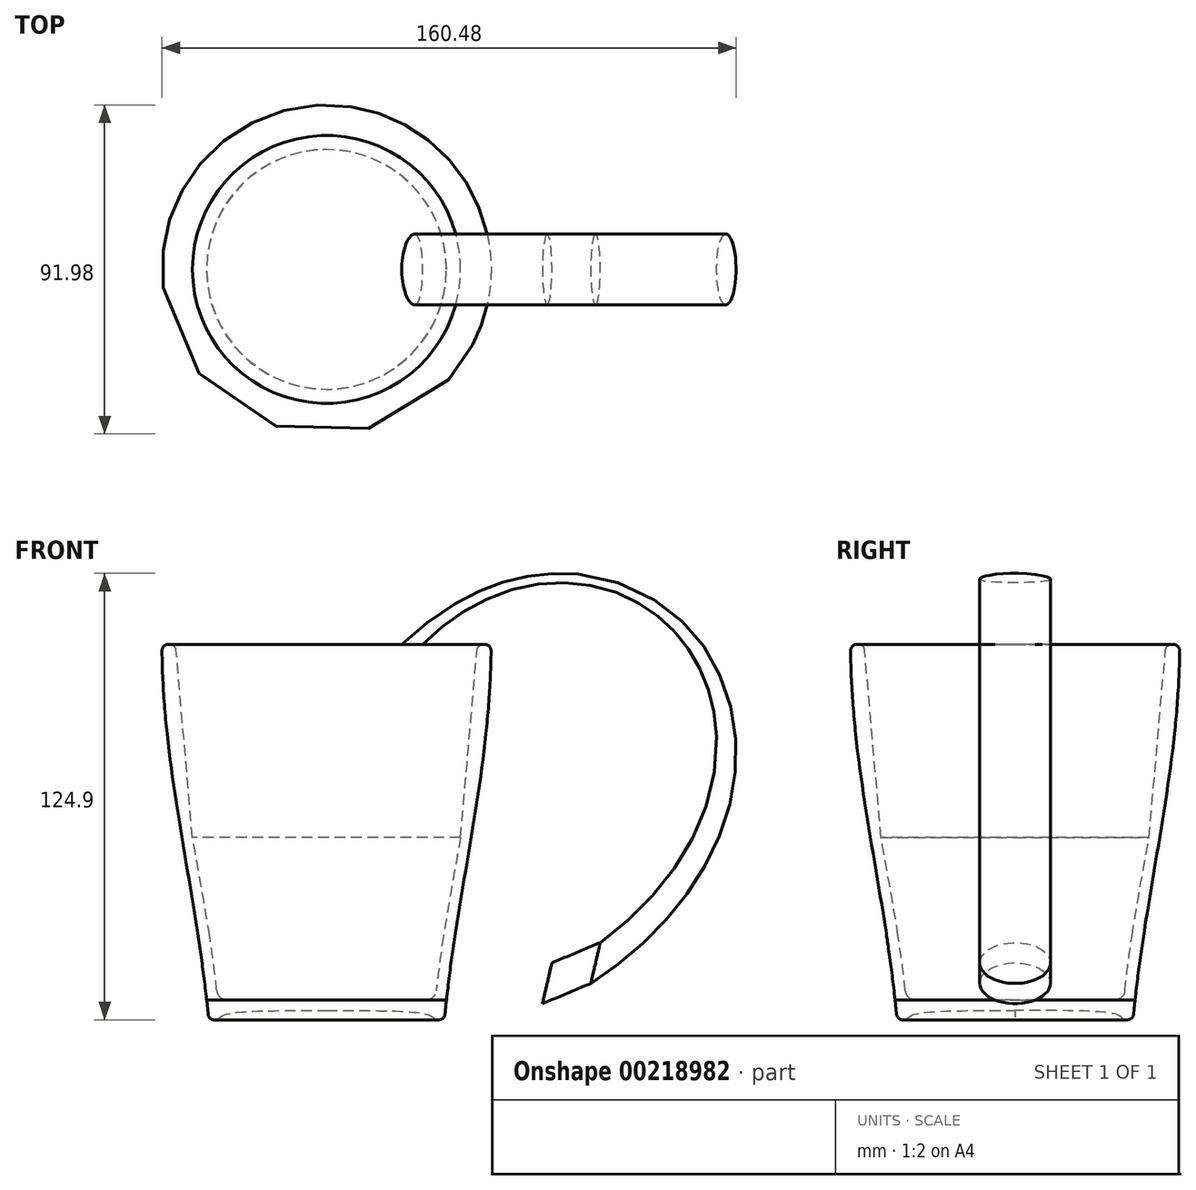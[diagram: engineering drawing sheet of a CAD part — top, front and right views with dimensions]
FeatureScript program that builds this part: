
annotation { "Feature Type Name" : "Feature", "Feature Type Description" : "" }
export const myFeature = defineFeature(function(context is Context, id is Id, definition is map)
    precondition{}
    {
        {
            assignVariable(context, id + "F0", {"name" : "handletop_r", "anyValue" : 4.46});
        }
        {
            var Q0;
            Q0=qCreatedBy(makeId("Front.planeOp"),FACE);
            var sketch = newSketch(context, id + "F1", { "sketchPlane" : qUnion([Q0])});
            skLineSegment(sketch, "E0.bottom", {"start": v(46, 52.5) * mm, "end": v(-46, 52.5) * mm});
            skLineSegment(sketch, "E0.top", {"start": v(46, -52.5) * mm, "end": v(-46, -52.5) * mm});
            skLineSegment(sketch, "E0.left", {"start": v(46, 52.5) * mm, "end": v(46, -52.5) * mm});
            skLineSegment(sketch, "E0.right", {"start": v(-46, 52.5) * mm, "end": v(-46, -52.5) * mm});
            skPoint(sketch, "E0.middle", {"position": v(0, 0) * mm});
            skLineSegment(sketch, "E1", {"start": v(33, -52.5) * mm, "end": v(46, 96.1) * mm});
            skFitSpline(sketch, "E2", {"points": [v(46, 52.5) * mm, v(33, -52.5) * mm], "startDerivative": vector(0, -106.58) * mm, "endDerivative": vector(-9.22, -105.38) * mm});
            skLineSegment(sketch, "E3.0", {"start": v(46, -49.9) * mm, "end": v(-46, -49.9) * mm});
            skLineSegment(sketch, "E4", {"start": v(0, 52.5) * mm, "end": v(0, -52.5) * mm});
            skLineSegment(sketch, "E5", {"start": v(30, -52.5) * mm, "end": v(30, -49.9) * mm});
            skFitSpline(sketch, "E6", {"points": [v(0, -49.9) * mm, v(30, -52.5) * mm], "startDerivative": vector(61.82, 0) * mm, "endDerivative": vector(0, -7.8) * mm});
            skFitSpline(sketch, "E7.0", {"points": [v(43, 52.5) * mm, v(43, 43.76) * mm, v(41.78, 26.36) * mm, v(37.8, 0.35) * mm, v(33.2, -25.76) * mm, v(30.79, -43.36) * mm, v(30.01, -52.24) * mm]});
            skLineSegment(sketch, "E8.0", {"start": v(46, -46.9) * mm, "end": v(-46, -46.9) * mm});
            skFitSpline(sketch, "E9", {"points": [v(44.56, 27.5) * mm, v(36.14, -27.5) * mm], "startDerivative": vector(116.8, 84.4) * mm, "endDerivative": vector(-197.13, -82.5) * mm});
            skLineSegment(sketch, "E10", {"start": v(44.56, 27.5) * mm, "end": v(30.84, 17.59) * mm});
            skLineSegment(sketch, "E11", {"start": v(36.14, -27.5) * mm, "end": v(22.63, -33.15) * mm});
            skSolve(sketch);
        }
        {
            var Q0;
            {var subQ1=sQuery(id+"F1.wireOp",EDGE,"E3.0");var subQ8=makeQuery(id+"F1.imprint","INTERSECT",VERTEX,{"derivedFrom":[subQ1,sQuery(id+"F1.wireOp",EDGE,"E5")]});Q0=makeQuery(id+"F1.imprint","IMPRINT",FACE,{"disambiguationData":[TD([[makeQuery(id+"F1.imprint","IMPRINT",EDGE,{"disambiguationData":[TD([[subQ8,1.0]])],"derivedFrom":subQ1}),-1.0]])]});}
            var Q1;
            {var subQ0=sQuery(id+"F1.wireOp",EDGE,"E5");Q1=makeQuery(id+"F1.imprint","IMPRINT",FACE,{"disambiguationData":[TD([[makeQuery(id+"F1.imprint","IMPRINT",EDGE,{"derivedFrom":subQ0}),-1.0]])]});}
            var Q2;
            {var subQ0=sQuery(id+"F1.wireOp",EDGE,"E5");Q2=makeQuery(id+"F1.imprint","IMPRINT",FACE,{"disambiguationData":[TD([[makeQuery(id+"F1.imprint","IMPRINT",EDGE,{"derivedFrom":subQ0}),1.0]])]});}
            var Q3;
            {var subQ0=sQuery(id+"F1.wireOp",EDGE,"E3.0");var subQ1=sQuery(id+"F1.wireOp",EDGE,"E1");var subQ2=makeQuery(id+"F1.imprint","INTERSECT",VERTEX,{"derivedFrom":[subQ1,subQ0]});Q3=makeQuery(id+"F1.imprint","IMPRINT",FACE,{"disambiguationData":[TD([[makeQuery(id+"F1.imprint","IMPRINT",EDGE,{"disambiguationData":[TD([[subQ2,-1.0]])],"derivedFrom":subQ1}),1.0]])]});}
            var Q4;
            {var subQ1=sQuery(id+"F1.wireOp",EDGE,"E0.bottom");var subQ3=sQuery(id+"F1.wireOp",EDGE,"E7.0");var subQ4=makeQuery(id+"F1.imprint","INTERSECT",VERTEX,{"derivedFrom":[subQ1,subQ3]});Q4=makeQuery(id+"F1.imprint","IMPRINT",FACE,{"disambiguationData":[TD([[makeQuery(id+"F1.imprint","IMPRINT",EDGE,{"disambiguationData":[TD([[subQ4,-1.0]])],"derivedFrom":subQ3}),1.0]])]});}
            var Q5;
            {var subQ0=sQuery(id+"F1.wireOp",EDGE,"E7.0");var subQ1=sQuery(id+"F1.wireOp",EDGE,"E0.bottom");var subQ2=makeQuery(id+"F1.imprint","INTERSECT",VERTEX,{"derivedFrom":[subQ1,subQ0]});Q5=makeQuery(id+"F1.imprint","IMPRINT",FACE,{"disambiguationData":[TD([[makeQuery(id+"F1.imprint","IMPRINT",EDGE,{"disambiguationData":[TD([[subQ2,-1.0]])],"derivedFrom":subQ1}),1.0]])]});}
            var Q6;
            {var subQ0=sQuery(id+"F1.wireOp",EDGE,"E10");var subQ1=sQuery(id+"F1.wireOp",EDGE,"E1");var subQ2=makeQuery(id+"F1.imprint","INTERSECT",VERTEX,{"derivedFrom":[subQ1,subQ0]});Q6=makeQuery(id+"F1.imprint","IMPRINT",FACE,{"disambiguationData":[TD([[makeQuery(id+"F1.imprint","IMPRINT",EDGE,{"disambiguationData":[TD([[subQ2,1.0]])],"derivedFrom":subQ1}),-1.0]])]});}
            var Q7;
            {var subQ0=sQuery(id+"F1.wireOp",EDGE,"E11");var subQ1=sQuery(id+"F1.wireOp",EDGE,"E1");var subQ2=makeQuery(id+"F1.imprint","INTERSECT",VERTEX,{"derivedFrom":[subQ1,subQ0]});Q7=makeQuery(id+"F1.imprint","IMPRINT",FACE,{"disambiguationData":[TD([[makeQuery(id+"F1.imprint","IMPRINT",EDGE,{"disambiguationData":[TD([[subQ2,-1.0]])],"derivedFrom":subQ1}),1.0]])]});}
            var Q8;
            {var subQ0=sQuery(id+"F1.wireOp",EDGE,"E8.0");var subQ1=sQuery(id+"F1.wireOp",EDGE,"E1");var subQ2=makeQuery(id+"F1.imprint","INTERSECT",VERTEX,{"derivedFrom":[subQ1,subQ0]});Q8=makeQuery(id+"F1.imprint","IMPRINT",FACE,{"disambiguationData":[TD([[makeQuery(id+"F1.imprint","IMPRINT",EDGE,{"disambiguationData":[TD([[subQ2,-1.0]])],"derivedFrom":subQ1}),1.0]])]});}
            var Q9;
            {var subQ1=sQuery(id+"F1.wireOp",EDGE,"E1");var subQ8=sQuery(id+"F1.wireOp",EDGE,"E11");var subQ10=makeQuery(id+"F1.imprint","INTERSECT",VERTEX,{"derivedFrom":[subQ1,subQ8]});Q9=makeQuery(id+"F1.imprint","IMPRINT",FACE,{"disambiguationData":[TD([[makeQuery(id+"F1.imprint","IMPRINT",EDGE,{"disambiguationData":[TD([[subQ10,-1.0]])],"derivedFrom":subQ1}),-1.0]])]});}
            var Q10;
            {var subQ0=sQuery(id+"F1.wireOp",EDGE,"E8.0");var subQ1=sQuery(id+"F1.wireOp",EDGE,"E1");var subQ2=makeQuery(id+"F1.imprint","INTERSECT",VERTEX,{"derivedFrom":[subQ1,subQ0]});Q10=makeQuery(id+"F1.imprint","IMPRINT",FACE,{"disambiguationData":[TD([[makeQuery(id+"F1.imprint","IMPRINT",EDGE,{"disambiguationData":[TD([[subQ2,-1.0]])],"derivedFrom":subQ1}),-1.0]])]});}
            var Q11;
            Q11=sQuery(id+"F1.wireOp",EDGE,"E4");
            revolve(context, id + "F2", {"entities" : qUnion([Q0, Q1, Q2, Q3, Q4, Q5, Q6, Q7, Q8, Q9, Q10]), "axis" : qUnion([Q11]), "revolveType" : RevolveType.FULL});
        }
        {
            var Q0;
            Q0=qCreatedBy(makeId("Right.planeOp"),FACE);
            cPlane(context, id + "F3", {"entities" : qUnion([Q0]), "cplaneType" : CPlaneType.OFFSET, "offset" : (getVariable(context, 'handletop_r')) * mm, "width" : 150 * mm, "height" : 150 * mm});
        }
        {
            var Q0;
            Q0=qCreatedBy(id+"F3.planeOp",FACE);
            var sketch = newSketch(context, id + "F4", { "sketchPlane" : qUnion([Q0])});
            skEllipse(sketch, "E12", {"center": v(0, 27.5) * mm, "majorRadius": 9.92 * mm, "minorRadius": 5.87 * mm, "majorAxis": v(-1, 0)});
            skSolve(sketch);
        }
        {
            var Q0;
            Q0=makeQuery(id+"F4.imprint","IMPRINT",FACE,{"disambiguationData":[TD([[makeQuery(id+"F4.imprint","IMPRINT",EDGE,{"derivedFrom":sQuery(id+"F4.wireOp",EDGE,"E12")}),1.0]])]});
            var Q1;
            Q1=sQuery(id+"F1.wireOp",EDGE,"E9");
            var Q2;
            Q2=sQuery(id+"F1.wireOp",EDGE,"E11");
            sweep(context, id + "F5", {"operationType" : NewBodyOperationType.ADD, "profiles" : qUnion([Q0]), "path" : qUnion([Q1, Q2])});
        }
        {
            var Q0;
            Q0=makeQuery(id+"F5.opSweep","CAP_FACE",FACE,{"disambiguationData":[OSD([sQuery(id+"F1.wireOp",VERTEX,"E9.start"),sQuery(id+"F4.wireOp",EDGE,"E12")])],"isStart":true});
            var Q1;
            Q1=sQuery(id+"F1.wireOp",EDGE,"E10");
            sweep(context, id + "F6", {"operationType" : NewBodyOperationType.ADD, "profiles" : qUnion([Q0]), "path" : qUnion([Q1])});
        }
        {
            var Q0;
            {var subQ1=sQuery(id+"F1.wireOp",EDGE,"E0.bottom");var subQ5=sQuery(id+"F1.wireOp",EDGE,"E4");var subQ10=makeQuery(id+"F1.imprint","INTERSECT",VERTEX,{"derivedFrom":[subQ1,subQ5]});Q0=makeQuery(id+"F1.imprint","IMPRINT",FACE,{"disambiguationData":[TD([[makeQuery(id+"F1.imprint","IMPRINT",EDGE,{"disambiguationData":[TD([[subQ10,1.0]])],"derivedFrom":subQ1}),1.0]])]});}
            var Q1;
            Q1=sQuery(id+"F1.wireOp",EDGE,"E4");
            revolve(context, id + "F7", {"operationType" : NewBodyOperationType.REMOVE, "entities" : qUnion([Q0]), "axis" : qUnion([Q1]), "revolveType" : RevolveType.FULL, "oppositeDirection" : true});
        }
        {
            var Q0;
            Q0=makeQuery(id+"F2.opRevolve","SWEPT_EDGE",EDGE,{"disambiguationData":[OSD([sQuery(id+"F1.wireOp",EDGE,"E0.bottom"),sQuery(id+"F1.wireOp",EDGE,"E1")])]});
            var Q1;
            Q1=makeQuery(id+"F2.opRevolve","SWEPT_EDGE",EDGE,{"disambiguationData":[OSD([sQuery(id+"F1.wireOp",EDGE,"E0.bottom"),sQuery(id+"F1.wireOp",EDGE,"E0.left"),sQuery(id+"F1.wireOp",EDGE,"E2")])]});
            var Q2;
            Q2=makeQuery(id+"F2.opRevolve","SWEPT_EDGE",EDGE,{"disambiguationData":[OSD([sQuery(id+"F1.wireOp",EDGE,"E0.top"),sQuery(id+"F1.wireOp",EDGE,"E5"),sQuery(id+"F1.wireOp",EDGE,"E6")])]});
            var Q3;
            Q3=makeQuery(id+"F2.opRevolve","SWEPT_EDGE",EDGE,{"disambiguationData":[OSD([sQuery(id+"F1.wireOp",EDGE,"E0.top"),sQuery(id+"F1.wireOp",EDGE,"E1"),sQuery(id+"F1.wireOp",EDGE,"E2")])]});
            fillet(context, id + "F8", {"entities" : qUnion([Q0, Q1, Q2, Q3]), "radius" : 1.75 * mm, "tangentPropagation" : true, "allowEdgeOverflow" : false});
        }
        {
            var Q0;
            Q0=makeQuery(id+"F2.opRevolve","SWEPT_EDGE",EDGE,{"disambiguationData":[OSD([sQuery(id+"F1.wireOp",EDGE,"E7.0"),sQuery(id+"F1.wireOp",EDGE,"E8.0")])]});
            fillet(context, id + "F9", {"entities" : qUnion([Q0]), "radius" : 2.75 * mm, "tangentPropagation" : true, "allowEdgeOverflow" : false});
        }
    });
